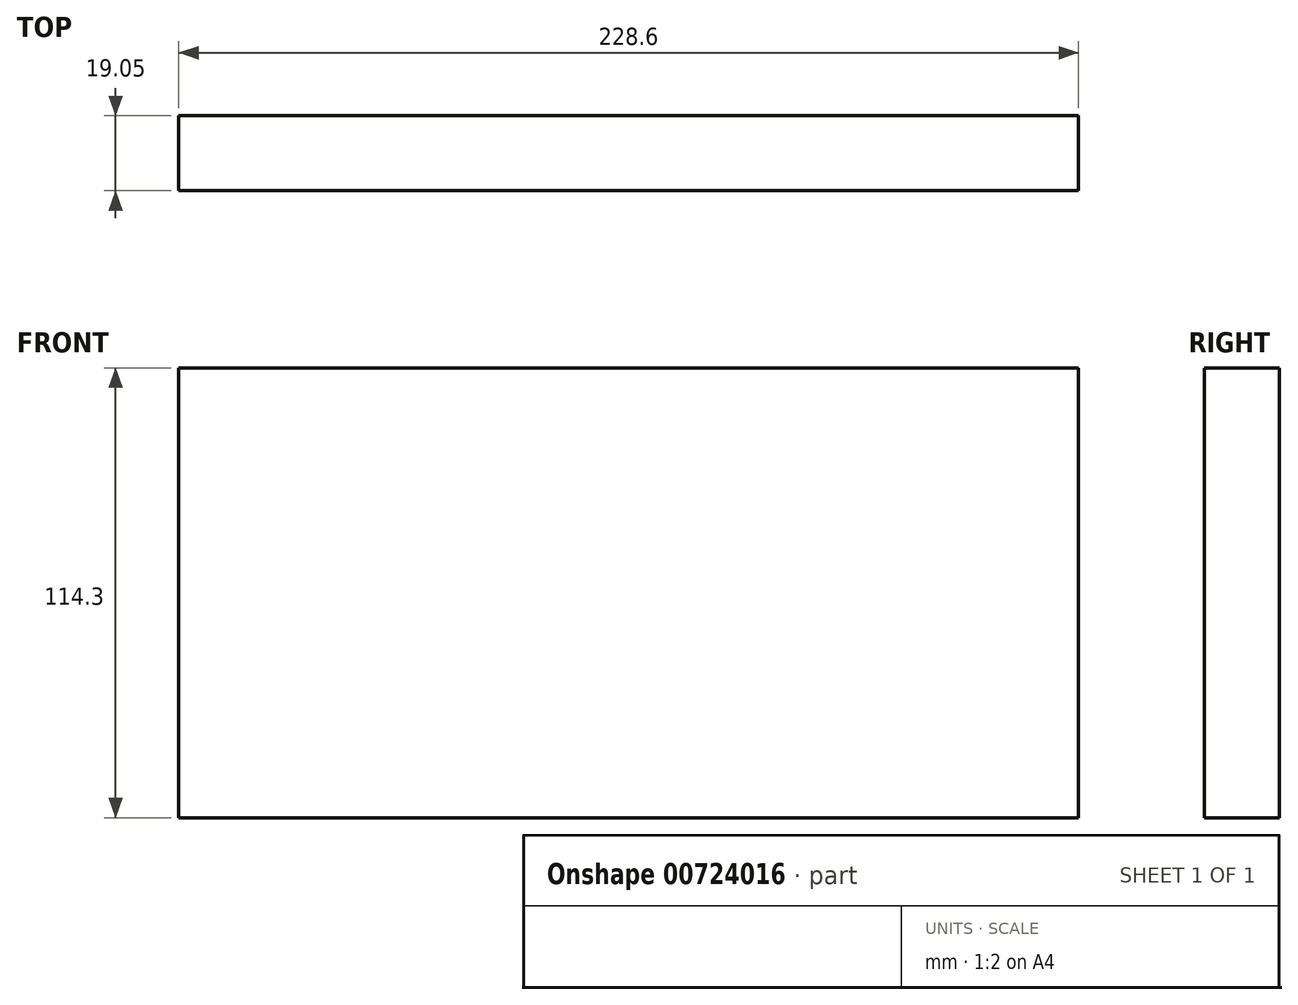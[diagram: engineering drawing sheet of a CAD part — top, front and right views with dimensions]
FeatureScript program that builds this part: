
annotation { "Feature Type Name" : "Feature", "Feature Type Description" : "" }
export const myFeature = defineFeature(function(context is Context, id is Id, definition is map)
    precondition{}
    {
        {
            var Q0;
            Q0=qCreatedBy(makeId("Front.planeOp"),FACE);
            var sketch = newSketch(context, id + "F0", { "sketchPlane" : qUnion([Q0])});
            skLineSegment(sketch, "E0.bottom", {"start": v(0, 0) * mm, "end": v(228.6, 0) * mm});
            skLineSegment(sketch, "E0.top", {"start": v(0, 114.3) * mm, "end": v(228.6, 114.3) * mm});
            skLineSegment(sketch, "E0.left", {"start": v(0, 0) * mm, "end": v(0, 114.3) * mm});
            skLineSegment(sketch, "E0.right", {"start": v(228.6, 0) * mm, "end": v(228.6, 114.3) * mm});
            skSolve(sketch);
        }
        {
            var Q0;
            Q0=makeQuery(id+"F0.imprint","IMPRINT",FACE,{"disambiguationData":[TD([[makeQuery(id+"F0.imprint","IMPRINT",EDGE,{"derivedFrom":sQuery(id+"F0.wireOp",EDGE,"E0.bottom")}),1.0]])]});
            extrude(context, id + "F1", {"entities" : qUnion([Q0]), "depth" : 19.05 * mm, "offsetDistance" : 25.4 * mm});
        }
    });
